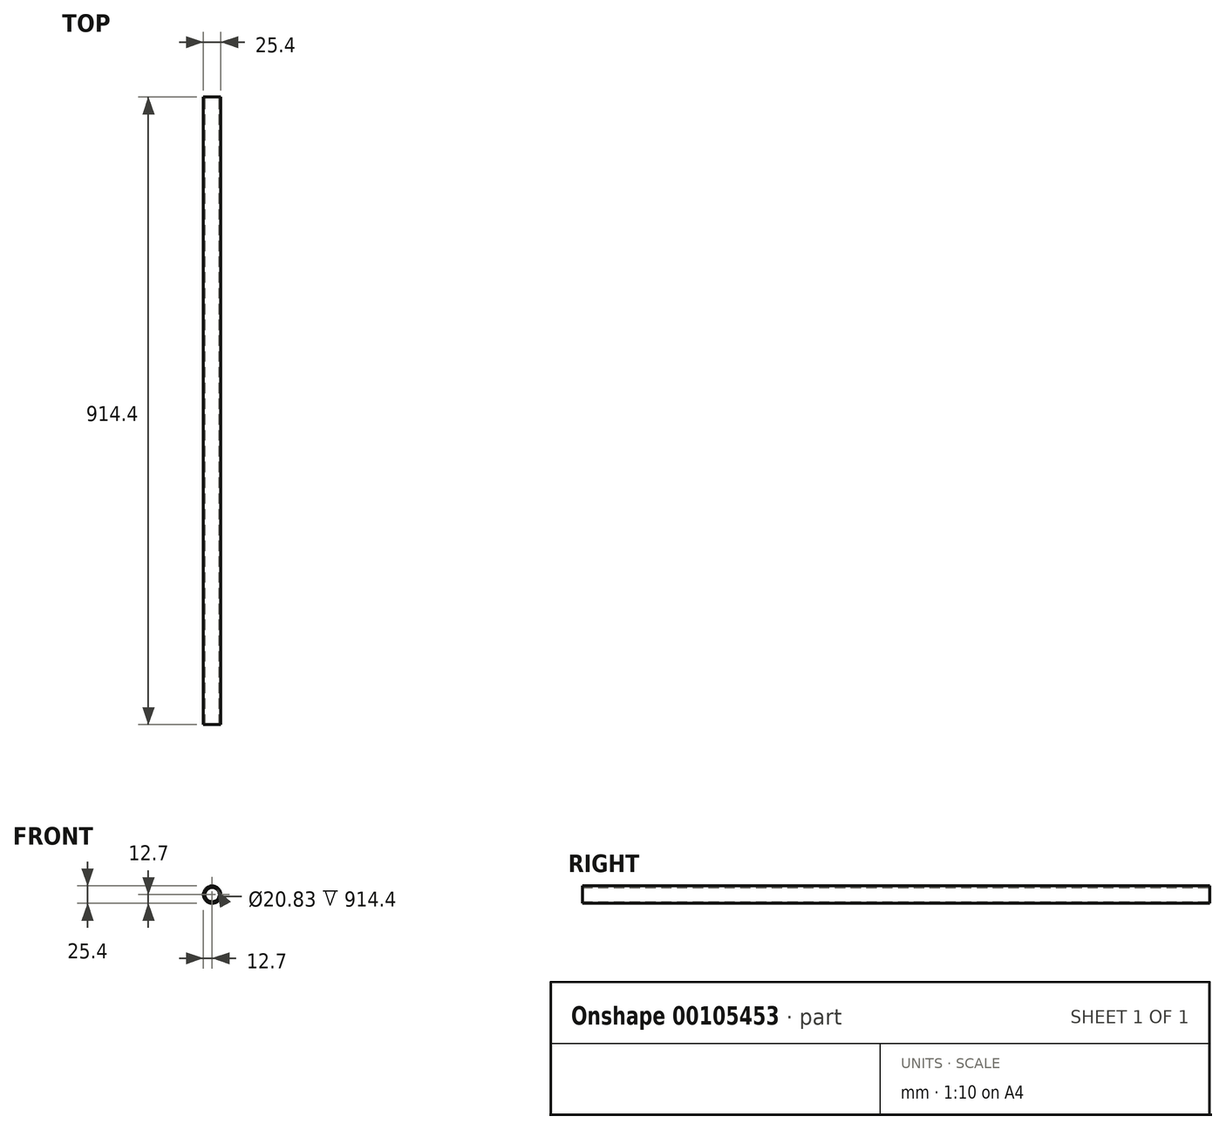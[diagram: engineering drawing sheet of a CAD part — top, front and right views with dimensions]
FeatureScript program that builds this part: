
annotation { "Feature Type Name" : "Feature", "Feature Type Description" : "" }
export const myFeature = defineFeature(function(context is Context, id is Id, definition is map)
    precondition{}
    {
        {
            var Q0;
            Q0=qCreatedBy(makeId("Front.planeOp"),FACE);
            var sketch = newSketch(context, id + "F0", { "sketchPlane" : qUnion([Q0])});
            skCircle(sketch, "E0", {"center": v(0, 0) * mm, "radius": 12.7 * mm});
            skCircle(sketch, "E1.0", {"center": v(0, 0) * mm, "radius": 10.41 * mm});
            skSolve(sketch);
        }
        {
            var Q0;
            Q0=makeQuery(id+"F0.imprint","IMPRINT",FACE,{"disambiguationData":[TD([[makeQuery(id+"F0.imprint","IMPRINT",EDGE,{"derivedFrom":sQuery(id+"F0.wireOp",EDGE,"E0")}),1.0]])]});
            extrude(context, id + "F1", {"entities" : qUnion([Q0]), "depth" : 914.4 * mm});
        }
    });
